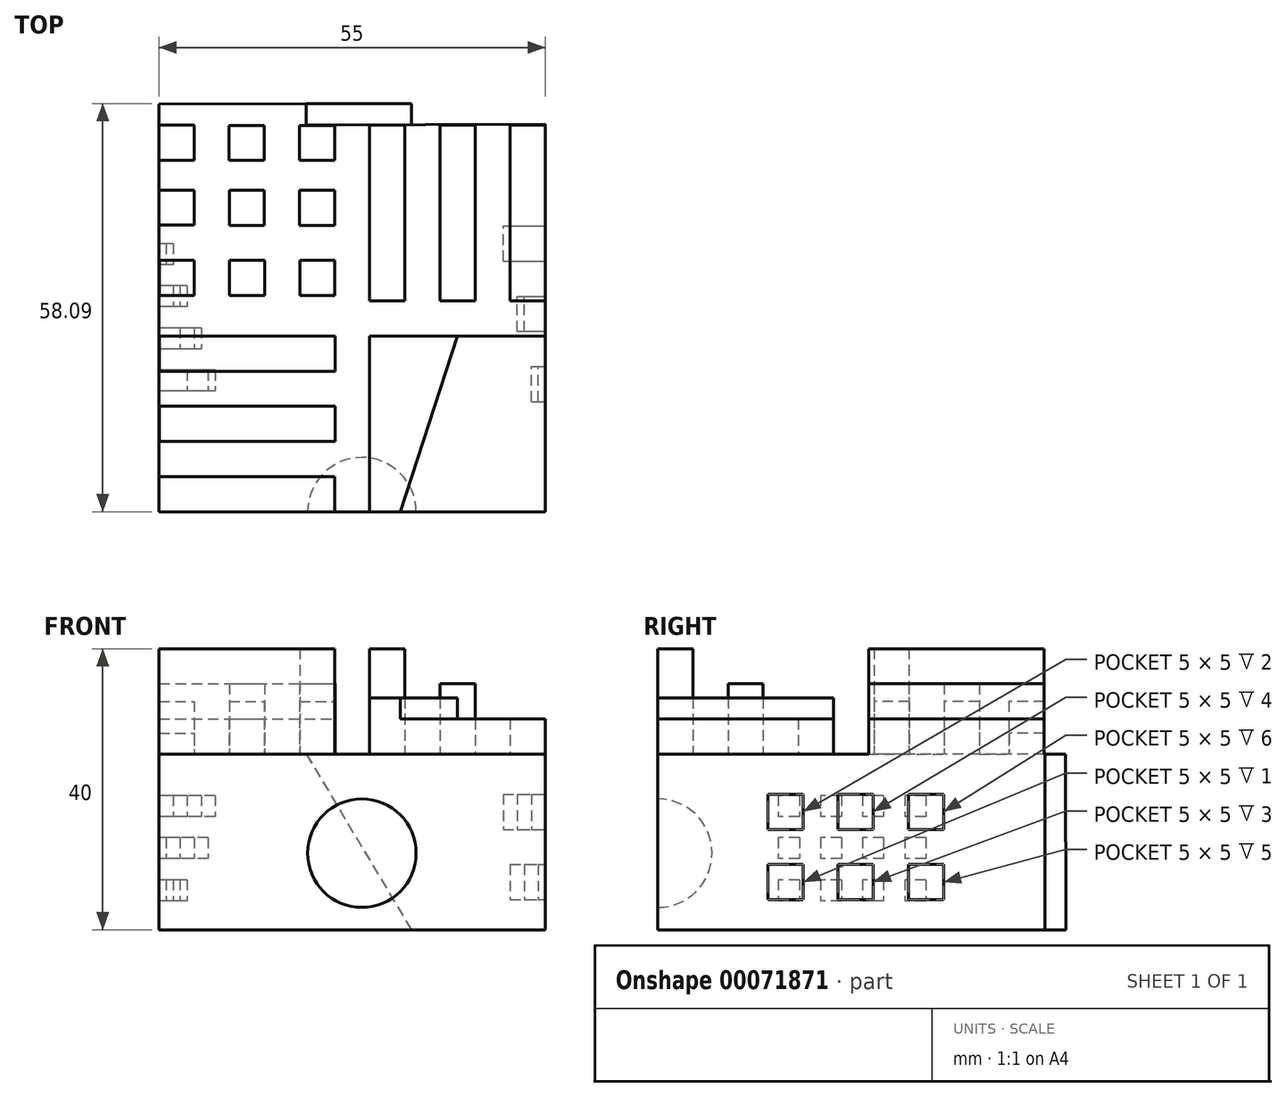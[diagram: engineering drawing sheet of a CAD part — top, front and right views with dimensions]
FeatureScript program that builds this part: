
annotation { "Feature Type Name" : "Feature", "Feature Type Description" : "" }
export const myFeature = defineFeature(function(context is Context, id is Id, definition is map)
    precondition{}
    {
        {
            var Q0;
            Q0=qCreatedBy(makeId("Top.planeOp"),FACE);
            var sketch = newSketch(context, id + "F0", { "sketchPlane" : qUnion([Q0])});
            skLineSegment(sketch, "E0.bottom", {"start": v(-30.94, 29.67) * mm, "end": v(-25.94, 29.67) * mm});
            skLineSegment(sketch, "E0.top", {"start": v(-30.94, 24.67) * mm, "end": v(-25.94, 24.67) * mm});
            skLineSegment(sketch, "E0.left", {"start": v(-30.94, 29.67) * mm, "end": v(-30.94, 24.67) * mm});
            skLineSegment(sketch, "E0.right", {"start": v(-25.94, 29.67) * mm, "end": v(-25.94, 24.67) * mm});
            skLineSegment(sketch, "E1.bottom", {"start": v(-0.94, 29.67) * mm, "end": v(4.06, 29.67) * mm});
            skLineSegment(sketch, "E1.top", {"start": v(-0.94, 4.67) * mm, "end": v(4.06, 4.67) * mm});
            skLineSegment(sketch, "E1.left", {"start": v(-0.94, 29.67) * mm, "end": v(-0.94, 4.67) * mm});
            skLineSegment(sketch, "E1.right", {"start": v(4.06, 29.67) * mm, "end": v(4.06, 4.67) * mm});
            skLineSegment(sketch, "E2.0.1.0", {"start": v(-0.94, 29.8) * mm, "end": v(4.06, 29.8) * mm});
            skLineSegment(sketch, "E2.0.1.1", {"start": v(-0.94, 29.8) * mm, "end": v(-0.94, 4.8) * mm});
            skLineSegment(sketch, "E2.0.1.2", {"start": v(4.06, 29.8) * mm, "end": v(4.06, 4.8) * mm});
            skLineSegment(sketch, "E2.1.0.0", {"start": v(9.06, 29.67) * mm, "end": v(14.06, 29.67) * mm});
            skLineSegment(sketch, "E2.1.0.1", {"start": v(9.06, 29.67) * mm, "end": v(9.06, 4.67) * mm});
            skLineSegment(sketch, "E2.1.0.2", {"start": v(14.06, 29.67) * mm, "end": v(14.06, 4.67) * mm});
            skLineSegment(sketch, "E2.1.0.3", {"start": v(9.06, 4.67) * mm, "end": v(14.06, 4.67) * mm});
            skLineSegment(sketch, "E2.1.1.0", {"start": v(9.06, 29.8) * mm, "end": v(14.06, 29.8) * mm});
            skLineSegment(sketch, "E2.1.1.1", {"start": v(9.06, 29.8) * mm, "end": v(9.06, 4.8) * mm});
            skLineSegment(sketch, "E2.1.1.2", {"start": v(14.06, 29.8) * mm, "end": v(14.06, 4.8) * mm});
            skLineSegment(sketch, "E2.2.0.0", {"start": v(19.06, 29.67) * mm, "end": v(24.06, 29.67) * mm});
            skLineSegment(sketch, "E2.2.0.1", {"start": v(19.06, 29.67) * mm, "end": v(19.06, 4.67) * mm});
            skLineSegment(sketch, "E2.2.0.2", {"start": v(24.06, 29.67) * mm, "end": v(24.06, 4.67) * mm});
            skLineSegment(sketch, "E2.2.0.3", {"start": v(19.06, 4.67) * mm, "end": v(24.06, 4.67) * mm});
            skLineSegment(sketch, "E2.2.1.0", {"start": v(19.06, 29.8) * mm, "end": v(24.06, 29.8) * mm});
            skLineSegment(sketch, "E2.2.1.1", {"start": v(19.06, 29.8) * mm, "end": v(19.06, 4.8) * mm});
            skLineSegment(sketch, "E2.2.1.2", {"start": v(24.06, 29.8) * mm, "end": v(24.06, 4.8) * mm});
            skLineSegment(sketch, "E2.direction1", {"start": v(-0.94, 29.67) * mm, "end": v(9.06, 29.67) * mm, "construction": true});
            skLineSegment(sketch, "E2.direction2", {"start": v(-0.94, 29.67) * mm, "end": v(-0.94, 29.8) * mm, "construction": true});
            skLineSegment(sketch, "E3.0.2.0", {"start": v(-30.94, -20.33) * mm, "end": v(-5.94, -20.33) * mm});
            skLineSegment(sketch, "E3.0.2.1", {"start": v(-30.94, -20.33) * mm, "end": v(-30.94, -25.33) * mm});
            skLineSegment(sketch, "E3.0.2.2", {"start": v(-30.94, -25.33) * mm, "end": v(-5.94, -25.33) * mm});
            skLineSegment(sketch, "E3.0.2.3", {"start": v(-5.94, -20.33) * mm, "end": v(-5.94, -25.33) * mm});
            skLineSegment(sketch, "E4.bottom", {"start": v(24.06, -25.33) * mm, "end": v(-0.94, -25.33) * mm});
            skLineSegment(sketch, "E4.top", {"start": v(24.06, -0.33) * mm, "end": v(-0.94, -0.33) * mm});
            skLineSegment(sketch, "E4.left", {"start": v(24.06, -25.33) * mm, "end": v(24.06, -0.33) * mm});
            skLineSegment(sketch, "E4.right", {"start": v(-0.94, -25.33) * mm, "end": v(-0.94, -0.33) * mm});
            skLineSegment(sketch, "E5", {"start": v(-30.94, 29.67) * mm, "end": v(24.06, 29.8) * mm});
            skLineSegment(sketch, "E6", {"start": v(24.06, 29.8) * mm, "end": v(24.06, -25.33) * mm});
            skLineSegment(sketch, "E7", {"start": v(24.06, -25.33) * mm, "end": v(-30.94, -25.33) * mm});
            skLineSegment(sketch, "E8", {"start": v(-30.94, 29.67) * mm, "end": v(-30.94, -25.33) * mm});
            skLineSegment(sketch, "E9.0.2.0", {"start": v(-30.88, -10.33) * mm, "end": v(-5.88, -10.33) * mm});
            skLineSegment(sketch, "E9.0.2.2", {"start": v(-30.88, -15.33) * mm, "end": v(-5.88, -15.33) * mm});
            skLineSegment(sketch, "E9.0.2.1", {"start": v(-30.88, -10.33) * mm, "end": v(-30.88, -15.33) * mm});
            skLineSegment(sketch, "E9.0.2.3", {"start": v(-5.88, -10.33) * mm, "end": v(-5.88, -15.33) * mm});
            skLineSegment(sketch, "E10.0.2.0", {"start": v(-30.88, -0.33) * mm, "end": v(-5.88, -0.33) * mm});
            skLineSegment(sketch, "E10.0.2.2", {"start": v(-30.88, -5.33) * mm, "end": v(-5.88, -5.33) * mm});
            skLineSegment(sketch, "E10.0.2.1", {"start": v(-30.88, -0.33) * mm, "end": v(-30.88, -5.33) * mm});
            skLineSegment(sketch, "E10.0.2.3", {"start": v(-5.88, -0.33) * mm, "end": v(-5.88, -5.33) * mm});
            skLineSegment(sketch, "E11", {"start": v(-30.88, -15.33) * mm, "end": v(-30.94, -20.33) * mm});
            skLineSegment(sketch, "E12.top", {"start": v(-20.94, 24.67) * mm, "end": v(-15.94, 24.67) * mm});
            skLineSegment(sketch, "E12.right", {"start": v(-15.94, 29.67) * mm, "end": v(-15.94, 24.67) * mm});
            skLineSegment(sketch, "E12.left", {"start": v(-20.94, 29.67) * mm, "end": v(-20.94, 24.67) * mm});
            skLineSegment(sketch, "E12.bottom", {"start": v(-20.94, 29.67) * mm, "end": v(-15.94, 29.67) * mm});
            skLineSegment(sketch, "E13.top", {"start": v(-10.94, 24.67) * mm, "end": v(-5.94, 24.67) * mm});
            skLineSegment(sketch, "E13.right", {"start": v(-5.94, 29.67) * mm, "end": v(-5.94, 24.67) * mm});
            skLineSegment(sketch, "E13.left", {"start": v(-10.94, 29.67) * mm, "end": v(-10.94, 24.67) * mm});
            skLineSegment(sketch, "E13.bottom", {"start": v(-10.94, 29.67) * mm, "end": v(-5.94, 29.67) * mm});
            skLineSegment(sketch, "E14", {"start": v(-25.94, 29.67) * mm, "end": v(-20.94, 29.67) * mm});
            skLineSegment(sketch, "E15.right", {"start": v(-5.93, 20.44) * mm, "end": v(-5.93, 15.44) * mm});
            skLineSegment(sketch, "E16.right", {"start": v(-15.93, 20.44) * mm, "end": v(-15.93, 15.44) * mm});
            skLineSegment(sketch, "E17.left", {"start": v(-30.93, 20.45) * mm, "end": v(-30.93, 15.45) * mm});
            skLineSegment(sketch, "E15.top", {"start": v(-10.93, 15.44) * mm, "end": v(-5.93, 15.44) * mm});
            skLineSegment(sketch, "E16.left", {"start": v(-20.93, 20.44) * mm, "end": v(-20.93, 15.44) * mm});
            skLineSegment(sketch, "E15.left", {"start": v(-10.93, 20.44) * mm, "end": v(-10.93, 15.44) * mm});
            skLineSegment(sketch, "E16.top", {"start": v(-20.93, 15.44) * mm, "end": v(-15.93, 15.44) * mm});
            skLineSegment(sketch, "E15.bottom", {"start": v(-10.93, 20.44) * mm, "end": v(-5.93, 20.44) * mm});
            skLineSegment(sketch, "E17.top", {"start": v(-30.93, 15.45) * mm, "end": v(-25.93, 15.45) * mm});
            skLineSegment(sketch, "E17.bottom", {"start": v(-30.93, 20.45) * mm, "end": v(-25.93, 20.45) * mm});
            skLineSegment(sketch, "E17.right", {"start": v(-25.93, 20.45) * mm, "end": v(-25.93, 15.45) * mm});
            skLineSegment(sketch, "E16.bottom", {"start": v(-20.93, 20.44) * mm, "end": v(-15.93, 20.44) * mm});
            skLineSegment(sketch, "E18.right", {"start": v(-5.9, 10.44) * mm, "end": v(-5.9, 5.44) * mm});
            skLineSegment(sketch, "E19.right", {"start": v(-15.9, 10.44) * mm, "end": v(-15.9, 5.44) * mm});
            skLineSegment(sketch, "E20.left", {"start": v(-30.9, 10.45) * mm, "end": v(-30.9, 5.45) * mm});
            skLineSegment(sketch, "E18.top", {"start": v(-10.9, 5.44) * mm, "end": v(-5.9, 5.44) * mm});
            skLineSegment(sketch, "E19.left", {"start": v(-20.9, 10.44) * mm, "end": v(-20.9, 5.44) * mm});
            skLineSegment(sketch, "E18.left", {"start": v(-10.9, 10.44) * mm, "end": v(-10.9, 5.44) * mm});
            skLineSegment(sketch, "E19.top", {"start": v(-20.9, 5.44) * mm, "end": v(-15.9, 5.44) * mm});
            skLineSegment(sketch, "E18.bottom", {"start": v(-10.9, 10.44) * mm, "end": v(-5.9, 10.44) * mm});
            skLineSegment(sketch, "E20.top", {"start": v(-30.9, 5.45) * mm, "end": v(-25.9, 5.45) * mm});
            skLineSegment(sketch, "E20.bottom", {"start": v(-30.9, 10.45) * mm, "end": v(-25.9, 10.45) * mm});
            skLineSegment(sketch, "E20.right", {"start": v(-25.9, 10.45) * mm, "end": v(-25.9, 5.45) * mm});
            skLineSegment(sketch, "E19.bottom", {"start": v(-20.9, 10.44) * mm, "end": v(-15.9, 10.44) * mm});
            skSolve(sketch);
        }
        {
            var Q0;
            {var subQ0=sQuery(id+"F0.wireOp",EDGE,"E4.right");Q0=makeQuery(id+"F0.imprint","IMPRINT",FACE,{"disambiguationData":[TD([[makeQuery(id+"F0.imprint","IMPRINT",EDGE,{"derivedFrom":subQ0}),-1.0]])]});}
            extrude(context, id + "F1", {"entities" : qUnion([Q0]), "depth" : 5 * mm});
        }
        {
            var Q0;
            {var subQ0=sQuery(id+"F0.wireOp",EDGE,"E3.0.2.0");Q0=makeQuery(id+"F0.imprint","IMPRINT",FACE,{"disambiguationData":[TD([[makeQuery(id+"F0.imprint","IMPRINT",EDGE,{"derivedFrom":subQ0}),-1.0]])]});}
            extrude(context, id + "F2", {"entities" : qUnion([Q0]), "depth" : 15 * mm});
        }
        {
            var Q0;
            Q0=qCreatedBy(makeId("Top.planeOp"),FACE);
            var sketch = newSketch(context, id + "F3", { "sketchPlane" : qUnion([Q0])});
            skLineSegment(sketch, "E21.0", {"start": v(24.06, -25.33) * mm, "end": v(-30.94, -25.33) * mm});
            skLineSegment(sketch, "E22.0", {"start": v(-30.94, 29.67) * mm, "end": v(-30.94, -25.33) * mm});
            skLineSegment(sketch, "E23.0", {"start": v(24.06, 29.8) * mm, "end": v(24.06, -25.33) * mm});
            skLineSegment(sketch, "E24.0", {"start": v(-30.94, 29.67) * mm, "end": v(24.06, 29.8) * mm});
            skSolve(sketch);
        }
        {
            var Q0;
            Q0=makeQuery(id+"F3.imprint","IMPRINT",FACE,{"disambiguationData":[TD([[makeQuery(id+"F3.imprint","IMPRINT",EDGE,{"derivedFrom":sQuery(id+"F3.wireOp",EDGE,"E21.0")}),-1.0]])]});
            extrude(context, id + "F4", {"entities" : qUnion([Q0]), "oppositeDirection" : true, "depth" : 25 * mm});
        }
        {
            var Q0;
            Q0=makeQuery(id+"F4.opExtrude","SWEPT_FACE",FACE,{"disambiguationData":[OSD([sQuery(id+"F3.wireOp",EDGE,"E21.0")])]});
            var sketch = newSketch(context, id + "F5", { "sketchPlane" : qUnion([Q0])});
            skCircle(sketch, "E25", {"center": v(-2.06, -14.08) * mm, "radius": 7.72 * mm});
            skLineSegment(sketch, "E26", {"start": v(-2.06, -6.36) * mm, "end": v(-2.06, -21.8) * mm});
            skSolve(sketch);
        }
        {
            var Q0;
            {var subQ0=sQuery(id+"F5.wireOp",EDGE,"E26");Q0=makeQuery(id+"F5.imprint","IMPRINT",FACE,{"disambiguationData":[TD([[makeQuery(id+"F5.imprint","IMPRINT",EDGE,{"derivedFrom":subQ0}),-1.0]])]});}
            var Q1;
            Q1=sQuery(id+"F5.wireOp",EDGE,"E26");
            revolve(context, id + "F6", {"operationType" : NewBodyOperationType.REMOVE, "entities" : qUnion([Q0]), "axis" : qUnion([Q1]), "revolveType" : RevolveType.FULL, "oppositeDirection" : true});
        }
        {
            var Q0;
            Q0=makeQuery(id+"F4.opExtrude","SWEPT_FACE",FACE,{"disambiguationData":[OSD([sQuery(id+"F3.wireOp",EDGE,"E22.0")])]});
            var sketch = newSketch(context, id + "F7", { "sketchPlane" : qUnion([Q0])});
            skLineSegment(sketch, "E27.bottom", {"start": v(-12.83, -5.88) * mm, "end": v(-9.83, -5.88) * mm});
            skLineSegment(sketch, "E27.top", {"start": v(-12.83, -8.88) * mm, "end": v(-9.83, -8.88) * mm});
            skLineSegment(sketch, "E27.left", {"start": v(-12.83, -5.88) * mm, "end": v(-12.83, -8.88) * mm});
            skLineSegment(sketch, "E27.right", {"start": v(-9.83, -5.88) * mm, "end": v(-9.83, -8.88) * mm});
            skLineSegment(sketch, "E28.0.1.0", {"start": v(-12.83, -11.88) * mm, "end": v(-12.83, -14.88) * mm});
            skLineSegment(sketch, "E28.0.1.1", {"start": v(-12.83, -14.88) * mm, "end": v(-9.83, -14.88) * mm});
            skLineSegment(sketch, "E28.0.1.2", {"start": v(-12.83, -11.88) * mm, "end": v(-9.83, -11.88) * mm});
            skLineSegment(sketch, "E28.0.1.3", {"start": v(-9.83, -11.88) * mm, "end": v(-9.83, -14.88) * mm});
            skLineSegment(sketch, "E28.0.2.0", {"start": v(-12.83, -17.88) * mm, "end": v(-12.83, -20.88) * mm});
            skLineSegment(sketch, "E28.0.2.1", {"start": v(-12.83, -20.88) * mm, "end": v(-9.83, -20.88) * mm});
            skLineSegment(sketch, "E28.0.2.2", {"start": v(-12.83, -17.88) * mm, "end": v(-9.83, -17.88) * mm});
            skLineSegment(sketch, "E28.0.2.3", {"start": v(-9.83, -17.88) * mm, "end": v(-9.83, -20.88) * mm});
            skLineSegment(sketch, "E28.1.0.0", {"start": v(-6.83, -5.88) * mm, "end": v(-6.83, -8.88) * mm});
            skLineSegment(sketch, "E28.1.0.1", {"start": v(-6.83, -8.88) * mm, "end": v(-3.83, -8.88) * mm});
            skLineSegment(sketch, "E28.1.0.2", {"start": v(-6.83, -5.88) * mm, "end": v(-3.83, -5.88) * mm});
            skLineSegment(sketch, "E28.1.0.3", {"start": v(-3.83, -5.88) * mm, "end": v(-3.83, -8.88) * mm});
            skLineSegment(sketch, "E28.1.1.0", {"start": v(-6.83, -11.88) * mm, "end": v(-6.83, -14.88) * mm});
            skLineSegment(sketch, "E28.1.1.1", {"start": v(-6.83, -14.88) * mm, "end": v(-3.83, -14.88) * mm});
            skLineSegment(sketch, "E28.1.1.2", {"start": v(-6.83, -11.88) * mm, "end": v(-3.83, -11.88) * mm});
            skLineSegment(sketch, "E28.1.1.3", {"start": v(-3.83, -11.88) * mm, "end": v(-3.83, -14.88) * mm});
            skLineSegment(sketch, "E28.1.2.0", {"start": v(-6.83, -17.88) * mm, "end": v(-6.83, -20.88) * mm});
            skLineSegment(sketch, "E28.1.2.1", {"start": v(-6.83, -20.88) * mm, "end": v(-3.83, -20.88) * mm});
            skLineSegment(sketch, "E28.1.2.2", {"start": v(-6.83, -17.88) * mm, "end": v(-3.83, -17.88) * mm});
            skLineSegment(sketch, "E28.1.2.3", {"start": v(-3.83, -17.88) * mm, "end": v(-3.83, -20.88) * mm});
            skLineSegment(sketch, "E28.2.0.0", {"start": v(-0.83, -5.88) * mm, "end": v(-0.83, -8.88) * mm});
            skLineSegment(sketch, "E28.2.0.1", {"start": v(-0.83, -8.88) * mm, "end": v(2.17, -8.88) * mm});
            skLineSegment(sketch, "E28.2.0.2", {"start": v(-0.83, -5.88) * mm, "end": v(2.17, -5.88) * mm});
            skLineSegment(sketch, "E28.2.0.3", {"start": v(2.17, -5.88) * mm, "end": v(2.17, -8.88) * mm});
            skLineSegment(sketch, "E28.2.1.0", {"start": v(-0.83, -11.88) * mm, "end": v(-0.83, -14.88) * mm});
            skLineSegment(sketch, "E28.2.1.1", {"start": v(-0.83, -14.88) * mm, "end": v(2.17, -14.88) * mm});
            skLineSegment(sketch, "E28.2.1.2", {"start": v(-0.83, -11.88) * mm, "end": v(2.17, -11.88) * mm});
            skLineSegment(sketch, "E28.2.1.3", {"start": v(2.17, -11.88) * mm, "end": v(2.17, -14.88) * mm});
            skLineSegment(sketch, "E28.2.2.0", {"start": v(-0.83, -17.88) * mm, "end": v(-0.83, -20.88) * mm});
            skLineSegment(sketch, "E28.2.2.1", {"start": v(-0.83, -20.88) * mm, "end": v(2.17, -20.88) * mm});
            skLineSegment(sketch, "E28.2.2.2", {"start": v(-0.83, -17.88) * mm, "end": v(2.17, -17.88) * mm});
            skLineSegment(sketch, "E28.2.2.3", {"start": v(2.17, -17.88) * mm, "end": v(2.17, -20.88) * mm});
            skLineSegment(sketch, "E28.3.0.0", {"start": v(5.17, -5.88) * mm, "end": v(5.17, -8.88) * mm});
            skLineSegment(sketch, "E28.3.0.1", {"start": v(5.17, -8.88) * mm, "end": v(8.17, -8.88) * mm});
            skLineSegment(sketch, "E28.3.0.2", {"start": v(5.17, -5.88) * mm, "end": v(8.17, -5.88) * mm});
            skLineSegment(sketch, "E28.3.0.3", {"start": v(8.17, -5.88) * mm, "end": v(8.17, -8.88) * mm});
            skLineSegment(sketch, "E28.3.1.0", {"start": v(5.17, -11.88) * mm, "end": v(5.17, -14.88) * mm});
            skLineSegment(sketch, "E28.3.1.1", {"start": v(5.17, -14.88) * mm, "end": v(8.17, -14.88) * mm});
            skLineSegment(sketch, "E28.3.1.2", {"start": v(5.17, -11.88) * mm, "end": v(8.17, -11.88) * mm});
            skLineSegment(sketch, "E28.3.1.3", {"start": v(8.17, -11.88) * mm, "end": v(8.17, -14.88) * mm});
            skLineSegment(sketch, "E28.3.2.0", {"start": v(5.17, -17.88) * mm, "end": v(5.17, -20.88) * mm});
            skLineSegment(sketch, "E28.3.2.1", {"start": v(5.17, -20.88) * mm, "end": v(8.17, -20.88) * mm});
            skLineSegment(sketch, "E28.3.2.2", {"start": v(5.17, -17.88) * mm, "end": v(8.17, -17.88) * mm});
            skLineSegment(sketch, "E28.3.2.3", {"start": v(8.17, -17.88) * mm, "end": v(8.17, -20.88) * mm});
            skLineSegment(sketch, "E28.direction1", {"start": v(-12.83, -8.88) * mm, "end": v(-6.83, -8.88) * mm, "construction": true});
            skLineSegment(sketch, "E28.direction2", {"start": v(-12.83, -8.88) * mm, "end": v(-12.83, -14.88) * mm, "construction": true});
            skSolve(sketch);
        }
        {
            var Q0;
            Q0=makeQuery(id+"F4.opExtrude","SWEPT_FACE",FACE,{"disambiguationData":[OSD([sQuery(id+"F3.wireOp",EDGE,"E23.0")])]});
            var sketch = newSketch(context, id + "F8", { "sketchPlane" : qUnion([Q0])});
            skLineSegment(sketch, "E29.bottom", {"start": v(-9.65, -5.71) * mm, "end": v(-4.65, -5.71) * mm});
            skLineSegment(sketch, "E29.top", {"start": v(-9.65, -10.71) * mm, "end": v(-4.65, -10.71) * mm});
            skLineSegment(sketch, "E29.left", {"start": v(-9.65, -5.71) * mm, "end": v(-9.65, -10.71) * mm});
            skLineSegment(sketch, "E29.right", {"start": v(-4.65, -5.71) * mm, "end": v(-4.65, -10.71) * mm});
            skLineSegment(sketch, "E30.0.1.0", {"start": v(-9.65, -15.71) * mm, "end": v(-4.65, -15.71) * mm});
            skLineSegment(sketch, "E30.0.1.1", {"start": v(-9.65, -20.71) * mm, "end": v(-4.65, -20.71) * mm});
            skLineSegment(sketch, "E30.0.1.2", {"start": v(-4.65, -15.71) * mm, "end": v(-4.65, -20.71) * mm});
            skLineSegment(sketch, "E30.0.1.3", {"start": v(-9.65, -15.71) * mm, "end": v(-9.65, -20.71) * mm});
            skLineSegment(sketch, "E30.1.0.0", {"start": v(0.35, -5.71) * mm, "end": v(5.35, -5.71) * mm});
            skLineSegment(sketch, "E30.1.0.1", {"start": v(0.35, -10.71) * mm, "end": v(5.35, -10.71) * mm});
            skLineSegment(sketch, "E30.1.0.2", {"start": v(5.35, -5.71) * mm, "end": v(5.35, -10.71) * mm});
            skLineSegment(sketch, "E30.1.0.3", {"start": v(0.35, -5.71) * mm, "end": v(0.35, -10.71) * mm});
            skLineSegment(sketch, "E30.1.1.0", {"start": v(0.35, -15.71) * mm, "end": v(5.35, -15.71) * mm});
            skLineSegment(sketch, "E30.1.1.1", {"start": v(0.35, -20.71) * mm, "end": v(5.35, -20.71) * mm});
            skLineSegment(sketch, "E30.1.1.2", {"start": v(5.35, -15.71) * mm, "end": v(5.35, -20.71) * mm});
            skLineSegment(sketch, "E30.1.1.3", {"start": v(0.35, -15.71) * mm, "end": v(0.35, -20.71) * mm});
            skLineSegment(sketch, "E30.2.0.0", {"start": v(10.35, -5.71) * mm, "end": v(15.35, -5.71) * mm});
            skLineSegment(sketch, "E30.2.0.1", {"start": v(10.35, -10.71) * mm, "end": v(15.35, -10.71) * mm});
            skLineSegment(sketch, "E30.2.0.2", {"start": v(15.35, -5.71) * mm, "end": v(15.35, -10.71) * mm});
            skLineSegment(sketch, "E30.2.0.3", {"start": v(10.35, -5.71) * mm, "end": v(10.35, -10.71) * mm});
            skLineSegment(sketch, "E30.2.1.0", {"start": v(10.35, -15.71) * mm, "end": v(15.35, -15.71) * mm});
            skLineSegment(sketch, "E30.2.1.1", {"start": v(10.35, -20.71) * mm, "end": v(15.35, -20.71) * mm});
            skLineSegment(sketch, "E30.2.1.2", {"start": v(15.35, -15.71) * mm, "end": v(15.35, -20.71) * mm});
            skLineSegment(sketch, "E30.2.1.3", {"start": v(10.35, -15.71) * mm, "end": v(10.35, -20.71) * mm});
            skLineSegment(sketch, "E30.direction1", {"start": v(-9.65, -5.71) * mm, "end": v(0.35, -5.71) * mm, "construction": true});
            skLineSegment(sketch, "E30.direction2", {"start": v(-9.65, -5.71) * mm, "end": v(-9.65, -15.71) * mm, "construction": true});
            skSolve(sketch);
        }
        {
            var Q0;
            Q0=makeQuery(id+"F8.imprint","IMPRINT",FACE,{"disambiguationData":[TD([[makeQuery(id+"F8.imprint","IMPRINT",EDGE,{"derivedFrom":sQuery(id+"F8.wireOp",EDGE,"E29.bottom")}),-1.0]])]});
            extrude(context, id + "F9", {"entities" : qUnion([Q0]), "operationType" : NewBodyOperationType.REMOVE, "oppositeDirection" : true, "depth" : 2 * mm});
        }
        {
            var Q0;
            {var subQ0=sQuery(id+"F0.wireOp",EDGE,"E0.bottom");Q0=makeQuery(id+"F0.imprint","IMPRINT",FACE,{"disambiguationData":[TD([[makeQuery(id+"F0.imprint","IMPRINT",EDGE,{"derivedFrom":subQ0}),-1.0]])]});}
            extrude(context, id + "F10", {"entities" : qUnion([Q0]), "operationType" : NewBodyOperationType.ADD, "depth" : 3 * mm});
        }
        {
            var Q0;
            {var subQ1=sQuery(id+"F0.wireOp",EDGE,"E2.1.0.0");Q0=makeQuery(id+"F0.imprint","IMPRINT",FACE,{"disambiguationData":[TD([[makeQuery(id+"F0.imprint","IMPRINT",EDGE,{"derivedFrom":subQ1}),-1.0]])]});}
            extrude(context, id + "F11", {"entities" : qUnion([Q0]), "operationType" : NewBodyOperationType.ADD, "depth" : 10 * mm});
        }
        {
            var Q0;
            {var subQ2=sQuery(id+"F0.wireOp",EDGE,"E2.2.0.0");Q0=makeQuery(id+"F0.imprint","IMPRINT",FACE,{"disambiguationData":[TD([[makeQuery(id+"F0.imprint","IMPRINT",EDGE,{"derivedFrom":subQ2}),-1.0]])]});}
            extrude(context, id + "F12", {"entities" : qUnion([Q0]), "operationType" : NewBodyOperationType.ADD, "depth" : 5 * mm});
        }
        {
            var Q0;
            Q0=makeQuery(id+"F8.imprint","IMPRINT",FACE,{"disambiguationData":[TD([[makeQuery(id+"F8.imprint","IMPRINT",EDGE,{"derivedFrom":sQuery(id+"F8.wireOp",EDGE,"E30.1.0.0")}),-1.0]])]});
            extrude(context, id + "F13", {"entities" : qUnion([Q0]), "operationType" : NewBodyOperationType.REMOVE, "oppositeDirection" : true, "depth" : 4 * mm});
        }
        {
            var Q0;
            Q0=makeQuery(id+"F8.imprint","IMPRINT",FACE,{"disambiguationData":[TD([[makeQuery(id+"F8.imprint","IMPRINT",EDGE,{"derivedFrom":sQuery(id+"F8.wireOp",EDGE,"E30.2.0.0")}),-1.0]])]});
            extrude(context, id + "F14", {"entities" : qUnion([Q0]), "operationType" : NewBodyOperationType.REMOVE, "oppositeDirection" : true, "depth" : 6 * mm});
        }
        {
            var Q0;
            Q0=makeQuery(id+"F8.imprint","IMPRINT",FACE,{"disambiguationData":[TD([[makeQuery(id+"F8.imprint","IMPRINT",EDGE,{"derivedFrom":sQuery(id+"F8.wireOp",EDGE,"E30.0.1.0")}),-1.0]])]});
            extrude(context, id + "F15", {"entities" : qUnion([Q0]), "operationType" : NewBodyOperationType.REMOVE, "oppositeDirection" : true, "depth" : 1 * mm});
        }
        {
            var Q0;
            Q0=makeQuery(id+"F8.imprint","IMPRINT",FACE,{"disambiguationData":[TD([[makeQuery(id+"F8.imprint","IMPRINT",EDGE,{"derivedFrom":sQuery(id+"F8.wireOp",EDGE,"E30.1.1.0")}),-1.0]])]});
            extrude(context, id + "F16", {"entities" : qUnion([Q0]), "operationType" : NewBodyOperationType.REMOVE, "oppositeDirection" : true, "depth" : 3 * mm});
        }
        {
            var Q0;
            Q0=makeQuery(id+"F8.imprint","IMPRINT",FACE,{"disambiguationData":[TD([[makeQuery(id+"F8.imprint","IMPRINT",EDGE,{"derivedFrom":sQuery(id+"F8.wireOp",EDGE,"E30.2.1.0")}),-1.0]])]});
            extrude(context, id + "F17", {"entities" : qUnion([Q0]), "operationType" : NewBodyOperationType.REMOVE, "oppositeDirection" : true, "depth" : 5 * mm});
        }
        {
            var Q0;
            Q0=makeQuery(id+"F7.imprint","IMPRINT",FACE,{"disambiguationData":[TD([[makeQuery(id+"F7.imprint","IMPRINT",EDGE,{"derivedFrom":sQuery(id+"F7.wireOp",EDGE,"E27.bottom")}),-1.0]])]});
            extrude(context, id + "F18", {"entities" : qUnion([Q0]), "operationType" : NewBodyOperationType.REMOVE, "oppositeDirection" : true, "depth" : 2 * mm});
        }
        {
            var Q0;
            Q0=makeQuery(id+"F7.imprint","IMPRINT",FACE,{"disambiguationData":[TD([[makeQuery(id+"F7.imprint","IMPRINT",EDGE,{"derivedFrom":sQuery(id+"F7.wireOp",EDGE,"E28.1.0.0")}),1.0]])]});
            extrude(context, id + "F19", {"entities" : qUnion([Q0]), "operationType" : NewBodyOperationType.REMOVE, "oppositeDirection" : true, "depth" : 4 * mm});
        }
        {
            var Q0;
            Q0=makeQuery(id+"F7.imprint","IMPRINT",FACE,{"disambiguationData":[TD([[makeQuery(id+"F7.imprint","IMPRINT",EDGE,{"derivedFrom":sQuery(id+"F7.wireOp",EDGE,"E28.2.0.0")}),1.0]])]});
            extrude(context, id + "F20", {"entities" : qUnion([Q0]), "operationType" : NewBodyOperationType.REMOVE, "oppositeDirection" : true, "depth" : 6 * mm});
        }
        {
            var Q0;
            Q0=makeQuery(id+"F7.imprint","IMPRINT",FACE,{"disambiguationData":[TD([[makeQuery(id+"F7.imprint","IMPRINT",EDGE,{"derivedFrom":sQuery(id+"F7.wireOp",EDGE,"E28.3.0.0")}),1.0]])]});
            extrude(context, id + "F21", {"entities" : qUnion([Q0]), "operationType" : NewBodyOperationType.REMOVE, "oppositeDirection" : true, "depth" : 8 * mm});
        }
        {
            var Q0;
            Q0=makeQuery(id+"F7.imprint","IMPRINT",FACE,{"disambiguationData":[TD([[makeQuery(id+"F7.imprint","IMPRINT",EDGE,{"derivedFrom":sQuery(id+"F7.wireOp",EDGE,"E28.0.1.0")}),1.0]])]});
            extrude(context, id + "F22", {"entities" : qUnion([Q0]), "operationType" : NewBodyOperationType.REMOVE, "oppositeDirection" : true, "depth" : 1 * mm});
        }
        {
            var Q0;
            Q0=makeQuery(id+"F7.imprint","IMPRINT",FACE,{"disambiguationData":[TD([[makeQuery(id+"F7.imprint","IMPRINT",EDGE,{"derivedFrom":sQuery(id+"F7.wireOp",EDGE,"E28.1.1.0")}),1.0]])]});
            extrude(context, id + "F23", {"entities" : qUnion([Q0]), "operationType" : NewBodyOperationType.REMOVE, "oppositeDirection" : true, "depth" : 3 * mm});
        }
        {
            var Q0;
            Q0=makeQuery(id+"F7.imprint","IMPRINT",FACE,{"disambiguationData":[TD([[makeQuery(id+"F7.imprint","IMPRINT",EDGE,{"derivedFrom":sQuery(id+"F7.wireOp",EDGE,"E28.2.1.0")}),1.0]])]});
            extrude(context, id + "F24", {"entities" : qUnion([Q0]), "operationType" : NewBodyOperationType.REMOVE, "oppositeDirection" : true, "depth" : 5 * mm});
        }
        {
            var Q0;
            Q0=makeQuery(id+"F7.imprint","IMPRINT",FACE,{"disambiguationData":[TD([[makeQuery(id+"F7.imprint","IMPRINT",EDGE,{"derivedFrom":sQuery(id+"F7.wireOp",EDGE,"E28.3.1.0")}),1.0]])]});
            extrude(context, id + "F25", {"entities" : qUnion([Q0]), "operationType" : NewBodyOperationType.REMOVE, "oppositeDirection" : true, "depth" : 7 * mm});
        }
        {
            var Q0;
            Q0=makeQuery(id+"F7.imprint","IMPRINT",FACE,{"disambiguationData":[TD([[makeQuery(id+"F7.imprint","IMPRINT",EDGE,{"derivedFrom":sQuery(id+"F7.wireOp",EDGE,"E28.0.2.0")}),1.0]])]});
            extrude(context, id + "F26", {"entities" : qUnion([Q0]), "operationType" : NewBodyOperationType.REMOVE, "oppositeDirection" : true, "depth" : 1 * mm});
        }
        {
            var Q0;
            Q0=makeQuery(id+"F7.imprint","IMPRINT",FACE,{"disambiguationData":[TD([[makeQuery(id+"F7.imprint","IMPRINT",EDGE,{"derivedFrom":sQuery(id+"F7.wireOp",EDGE,"E28.1.2.0")}),1.0]])]});
            extrude(context, id + "F27", {"entities" : qUnion([Q0]), "operationType" : NewBodyOperationType.REMOVE, "oppositeDirection" : true, "depth" : 2 * mm});
        }
        {
            var Q0;
            Q0=makeQuery(id+"F7.imprint","IMPRINT",FACE,{"disambiguationData":[TD([[makeQuery(id+"F7.imprint","IMPRINT",EDGE,{"derivedFrom":sQuery(id+"F7.wireOp",EDGE,"E28.2.2.0")}),1.0]])]});
            extrude(context, id + "F28", {"entities" : qUnion([Q0]), "operationType" : NewBodyOperationType.REMOVE, "oppositeDirection" : true, "depth" : 3 * mm});
        }
        {
            var Q0;
            Q0=makeQuery(id+"F7.imprint","IMPRINT",FACE,{"disambiguationData":[TD([[makeQuery(id+"F7.imprint","IMPRINT",EDGE,{"derivedFrom":sQuery(id+"F7.wireOp",EDGE,"E28.3.2.0")}),1.0]])]});
            extrude(context, id + "F29", {"entities" : qUnion([Q0]), "operationType" : NewBodyOperationType.REMOVE, "oppositeDirection" : true, "depth" : 4 * mm});
        }
        {
            var Q0;
            Q0=makeQuery(id+"F1.opExtrude","CAP_FACE",FACE,{"disambiguationData":[OSD([sQuery(id+"F0.wireOp",EDGE,"E4.top"),sQuery(id+"F0.wireOp",EDGE,"E4.right"),sQuery(id+"F0.wireOp",EDGE,"E6"),sQuery(id+"F0.wireOp",EDGE,"E7")])],"isStart":false});
            var sketch = newSketch(context, id + "F30", { "sketchPlane" : qUnion([Q0])});
            skLineSegment(sketch, "E31", {"start": v(3.4, -25.33) * mm, "end": v(11.56, -0.33) * mm});
            skPoint(sketch, "E31.endSnap0", {"position": v(11.56, -25.33) * mm});
            skSolve(sketch);
        }
        {
            var Q0;
            {var subQ0=sQuery(id+"F30.wireOp",EDGE,"E31");Q0=makeQuery(id+"F30.imprint","IMPRINT",FACE,{"disambiguationData":[TD([[makeQuery(id+"F30.imprint","IMPRINT",EDGE,{"derivedFrom":subQ0}),1.0]])]});}
            extrude(context, id + "F31", {"entities" : qUnion([Q0]), "operationType" : NewBodyOperationType.ADD, "depth" : 3 * mm});
        }
        {
            var Q0;
            Q0=makeQuery(id+"F4.opExtrude","SWEPT_FACE",FACE,{"disambiguationData":[OSD([sQuery(id+"F3.wireOp",EDGE,"E24.0")])]});
            var sketch = newSketch(context, id + "F32", { "sketchPlane" : qUnion([Q0])});
            skLineSegment(sketch, "E32", {"start": v(9.88, 0) * mm, "end": v(-5.06, -25) * mm});
            skSolve(sketch);
        }
        {
            var Q0;
            {var subQ0=sQuery(id+"F32.wireOp",EDGE,"E32");Q0=makeQuery(id+"F32.imprint","IMPRINT",FACE,{"disambiguationData":[TD([[makeQuery(id+"F32.imprint","IMPRINT",EDGE,{"derivedFrom":subQ0}),1.0]])]});}
            extrude(context, id + "F33", {"entities" : qUnion([Q0]), "operationType" : NewBodyOperationType.ADD, "depth" : 3 * mm});
        }
        {
            var Q0;
            {var subQ2=sQuery(id+"F0.wireOp",EDGE,"E1.bottom");Q0=makeQuery(id+"F0.imprint","IMPRINT",FACE,{"disambiguationData":[TD([[makeQuery(id+"F0.imprint","IMPRINT",EDGE,{"derivedFrom":subQ2}),-1.0]])]});}
            extrude(context, id + "F34", {"entities" : qUnion([Q0]), "operationType" : NewBodyOperationType.ADD, "depth" : 15 * mm});
        }
        {
            var Q0;
            Q0=makeQuery(id+"F0.imprint","IMPRINT",FACE,{"disambiguationData":[TD([[makeQuery(id+"F0.imprint","IMPRINT",EDGE,{"derivedFrom":sQuery(id+"F0.wireOp",EDGE,"E9.0.2.0")}),-1.0]])]});
            extrude(context, id + "F35", {"entities" : qUnion([Q0]), "operationType" : NewBodyOperationType.ADD, "depth" : 10 * mm});
        }
        {
            var Q0;
            Q0=makeQuery(id+"F0.imprint","IMPRINT",FACE,{"disambiguationData":[TD([[makeQuery(id+"F0.imprint","IMPRINT",EDGE,{"derivedFrom":sQuery(id+"F0.wireOp",EDGE,"E10.0.2.0")}),-1.0]])]});
            extrude(context, id + "F36", {"entities" : qUnion([Q0]), "operationType" : NewBodyOperationType.ADD, "depth" : 5 * mm});
        }
        {
            var Q0;
            Q0=makeQuery(id+"F0.imprint","IMPRINT",FACE,{"disambiguationData":[TD([[makeQuery(id+"F0.imprint","IMPRINT",EDGE,{"derivedFrom":sQuery(id+"F0.wireOp",EDGE,"E18.right")}),-1.0]])]});
            extrude(context, id + "F37", {"entities" : qUnion([Q0]), "operationType" : NewBodyOperationType.ADD, "depth" : 15 * mm});
        }
        {
            var Q0;
            Q0=makeQuery(id+"F0.imprint","IMPRINT",FACE,{"disambiguationData":[TD([[makeQuery(id+"F0.imprint","IMPRINT",EDGE,{"derivedFrom":sQuery(id+"F0.wireOp",EDGE,"E15.right")}),-1.0]])]});
            extrude(context, id + "F38", {"entities" : qUnion([Q0]), "operationType" : NewBodyOperationType.ADD, "depth" : 10 * mm});
        }
        {
            var Q0;
            Q0=makeQuery(id+"F0.imprint","IMPRINT",FACE,{"disambiguationData":[TD([[makeQuery(id+"F0.imprint","IMPRINT",EDGE,{"derivedFrom":sQuery(id+"F0.wireOp",EDGE,"E19.right")}),-1.0]])]});
            extrude(context, id + "F39", {"entities" : qUnion([Q0]), "operationType" : NewBodyOperationType.ADD, "depth" : 10 * mm});
        }
        {
            var Q0;
            Q0=makeQuery(id+"F0.imprint","IMPRINT",FACE,{"disambiguationData":[TD([[makeQuery(id+"F0.imprint","IMPRINT",EDGE,{"derivedFrom":sQuery(id+"F0.wireOp",EDGE,"E13.top")}),1.0]])]});
            extrude(context, id + "F40", {"entities" : qUnion([Q0]), "operationType" : NewBodyOperationType.ADD, "depth" : 7.5 * mm});
        }
        {
            var Q0;
            Q0=makeQuery(id+"F0.imprint","IMPRINT",FACE,{"disambiguationData":[TD([[makeQuery(id+"F0.imprint","IMPRINT",EDGE,{"derivedFrom":sQuery(id+"F0.wireOp",EDGE,"E16.right")}),-1.0]])]});
            extrude(context, id + "F41", {"entities" : qUnion([Q0]), "operationType" : NewBodyOperationType.ADD, "depth" : 7.5 * mm});
        }
        {
            var Q0;
            Q0=makeQuery(id+"F0.imprint","IMPRINT",FACE,{"disambiguationData":[TD([[makeQuery(id+"F0.imprint","IMPRINT",EDGE,{"derivedFrom":sQuery(id+"F0.wireOp",EDGE,"E20.left")}),1.0]])]});
            extrude(context, id + "F42", {"entities" : qUnion([Q0]), "operationType" : NewBodyOperationType.ADD, "depth" : 7.5 * mm});
        }
        {
            var Q0;
            Q0=makeQuery(id+"F0.imprint","IMPRINT",FACE,{"disambiguationData":[TD([[makeQuery(id+"F0.imprint","IMPRINT",EDGE,{"derivedFrom":sQuery(id+"F0.wireOp",EDGE,"E12.top")}),1.0]])]});
            extrude(context, id + "F43", {"entities" : qUnion([Q0]), "operationType" : NewBodyOperationType.ADD, "depth" : 5 * mm});
        }
        {
            var Q0;
            Q0=makeQuery(id+"F0.imprint","IMPRINT",FACE,{"disambiguationData":[TD([[makeQuery(id+"F0.imprint","IMPRINT",EDGE,{"derivedFrom":sQuery(id+"F0.wireOp",EDGE,"E17.left")}),1.0]])]});
            extrude(context, id + "F44", {"entities" : qUnion([Q0]), "operationType" : NewBodyOperationType.ADD, "depth" : 5 * mm});
        }
    });
